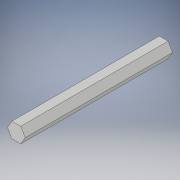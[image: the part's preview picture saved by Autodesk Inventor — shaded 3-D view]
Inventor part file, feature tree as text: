
AUTODESK INVENTOR PART (.ipt)
format: ipt  version: 2018 (Build 220112000, 112)  size: 94,720 bytes
history: native  units: in
note: dims shown in document units (in); Inventor stores cm internally (conversion verified against a paired STEP export)
features: extrude x1, sketch x1
ambient origin geometry x8: Origin, YZ Plane, XZ Plane, XY Plane, X Axis, Y Axis, Z Axis, Center Point
bodies: Solid1 (feature_tree)
feature tree (2):
  extrude  "Extrusion1"  Depth=4.8125in TaperAngle=0.0deg
  sketch  "Sketch1"  dims[d0=0.5in d1=4.8125in d2=0.0in]
